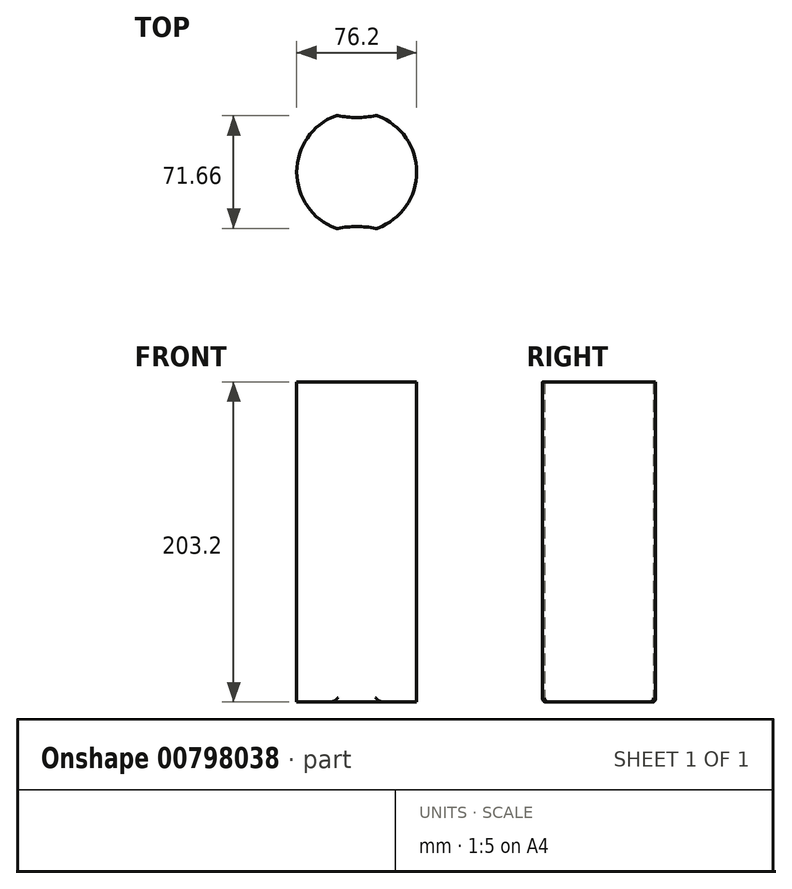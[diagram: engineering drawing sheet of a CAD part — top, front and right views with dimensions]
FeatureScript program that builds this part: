
annotation { "Feature Type Name" : "Feature", "Feature Type Description" : "" }
export const myFeature = defineFeature(function(context is Context, id is Id, definition is map)
    precondition{}
    {
        {
            var Q0;
            Q0=qCreatedBy(makeId("Top.planeOp"),FACE);
            var sketch = newSketch(context, id + "F0", { "sketchPlane" : qUnion([Q0])});
            skCircle(sketch, "E0", {"center": v(0, 0) * mm, "radius": 38.1 * mm});
            skLineSegment(sketch, "E1", {"start": v(-12.7, 35.92) * mm, "end": v(12.7, 35.92) * mm});
            skArc(sketch, "E2", {"start": v(-12.7, 35.92) * mm, "mid": v(0, 34.64) * mm, "end": v(12.7, 35.92) * mm});
            skArc(sketch, "E3.MirrorCS", {"start": v(-12.7, -35.92) * mm, "mid": v(0, -34.64) * mm, "end": v(12.7, -35.92) * mm});
            skSolve(sketch);
        }
        {
            var Q0;
            {var subQ0=sQuery(id+"F0.wireOp",EDGE,"E2");Q0=makeQuery(id+"F0.imprint","IMPRINT",FACE,{"disambiguationData":[TD([[makeQuery(id+"F0.imprint","IMPRINT",EDGE,{"derivedFrom":subQ0}),-1.0]])]});}
            extrude(context, id + "F1", {"entities" : qUnion([Q0]), "depth" : 203.2 * mm, "offsetDistance" : 25.4 * mm});
        }
        {
            var Q0;
            {var subQ0=sQuery(id+"F0.wireOp",EDGE,"E0");Q0=makeQuery(id+"F1.opExtrude","CAP_EDGE",EDGE,{"disambiguationData":[OSD([subQ0]),TDD([makeQuery(id+"F0.imprint","IMPRINT",EDGE,{"disambiguationData":[TD([[makeQuery(id+"F0.imprint","INTERSECT",VERTEX,{"disambiguationData":[OD(1.0)],"derivedFrom":[subQ0,sQuery(id+"F0.wireOp",EDGE,"E3.MirrorCS")]}),-1.0]])],"derivedFrom":subQ0})])],"isStart":true});}
            var Q1;
            Q1=makeQuery(id+"F1.opExtrude","CAP_EDGE",EDGE,{"disambiguationData":[OSD([sQuery(id+"F0.wireOp",EDGE,"E2")])],"isStart":true});
            var Q2;
            {var subQ0=sQuery(id+"F0.wireOp",EDGE,"E0");Q2=makeQuery(id+"F1.opExtrude","CAP_EDGE",EDGE,{"disambiguationData":[OSD([subQ0]),TDD([makeQuery(id+"F0.imprint","IMPRINT",EDGE,{"disambiguationData":[TD([[makeQuery(id+"F0.imprint","INTERSECT",VERTEX,{"disambiguationData":[OD(0.0)],"derivedFrom":[subQ0,sQuery(id+"F0.wireOp",EDGE,"E3.MirrorCS")]}),1.0]])],"derivedFrom":subQ0})])],"isStart":true});}
            var Q3;
            Q3=makeQuery(id+"F1.opExtrude","CAP_EDGE",EDGE,{"disambiguationData":[OSD([sQuery(id+"F0.wireOp",EDGE,"E3.MirrorCS")])],"isStart":true});
            var Q4;
            {var subQ0=sQuery(id+"F0.wireOp",EDGE,"E3.MirrorCS");var subQ1=sQuery(id+"F0.wireOp",EDGE,"E0");Q4=makeQuery(id+"F1.opExtrude","SWEPT_EDGE",EDGE,{"disambiguationData":[OSD([subQ1,subQ0]),TDD([makeQuery(id+"F0.imprint","INTERSECT",VERTEX,{"disambiguationData":[OD(0.0)],"derivedFrom":[subQ1,subQ0]})])]});}
            var Q5;
            {var subQ0=sQuery(id+"F0.wireOp",EDGE,"E3.MirrorCS");var subQ1=sQuery(id+"F0.wireOp",EDGE,"E0");Q5=makeQuery(id+"F1.opExtrude","SWEPT_EDGE",EDGE,{"disambiguationData":[OSD([subQ1,subQ0]),TDD([makeQuery(id+"F0.imprint","INTERSECT",VERTEX,{"disambiguationData":[OD(1.0)],"derivedFrom":[subQ1,subQ0]})])]});}
            var Q6;
            {var subQ0=sQuery(id+"F0.wireOp",EDGE,"E2");var subQ1=sQuery(id+"F0.wireOp",EDGE,"E1");var subQ2=sQuery(id+"F0.wireOp",EDGE,"E0");Q6=makeQuery(id+"F1.opExtrude","SWEPT_EDGE",EDGE,{"disambiguationData":[OSD([subQ2,subQ1,subQ0]),TDD([makeQuery(id+"F0.imprint","INTERSECT",VERTEX,{"disambiguationData":[OD(0.0)],"derivedFrom":[subQ2,subQ1,subQ0]})])]});}
            var Q7;
            {var subQ0=sQuery(id+"F0.wireOp",EDGE,"E2");var subQ1=sQuery(id+"F0.wireOp",EDGE,"E1");var subQ2=sQuery(id+"F0.wireOp",EDGE,"E0");Q7=makeQuery(id+"F1.opExtrude","SWEPT_EDGE",EDGE,{"disambiguationData":[OSD([subQ2,subQ1,subQ0]),TDD([makeQuery(id+"F0.imprint","INTERSECT",VERTEX,{"disambiguationData":[OD(1.0)],"derivedFrom":[subQ2,subQ1,subQ0]})])]});}
            fillet(context, id + "F2", {"entities" : qUnion([Q0, Q1, Q2, Q3, Q4, Q5, Q6, Q7]), "radius" : 2.54 * mm, "tangentPropagation" : true, "allowEdgeOverflow" : false});
        }
    });
